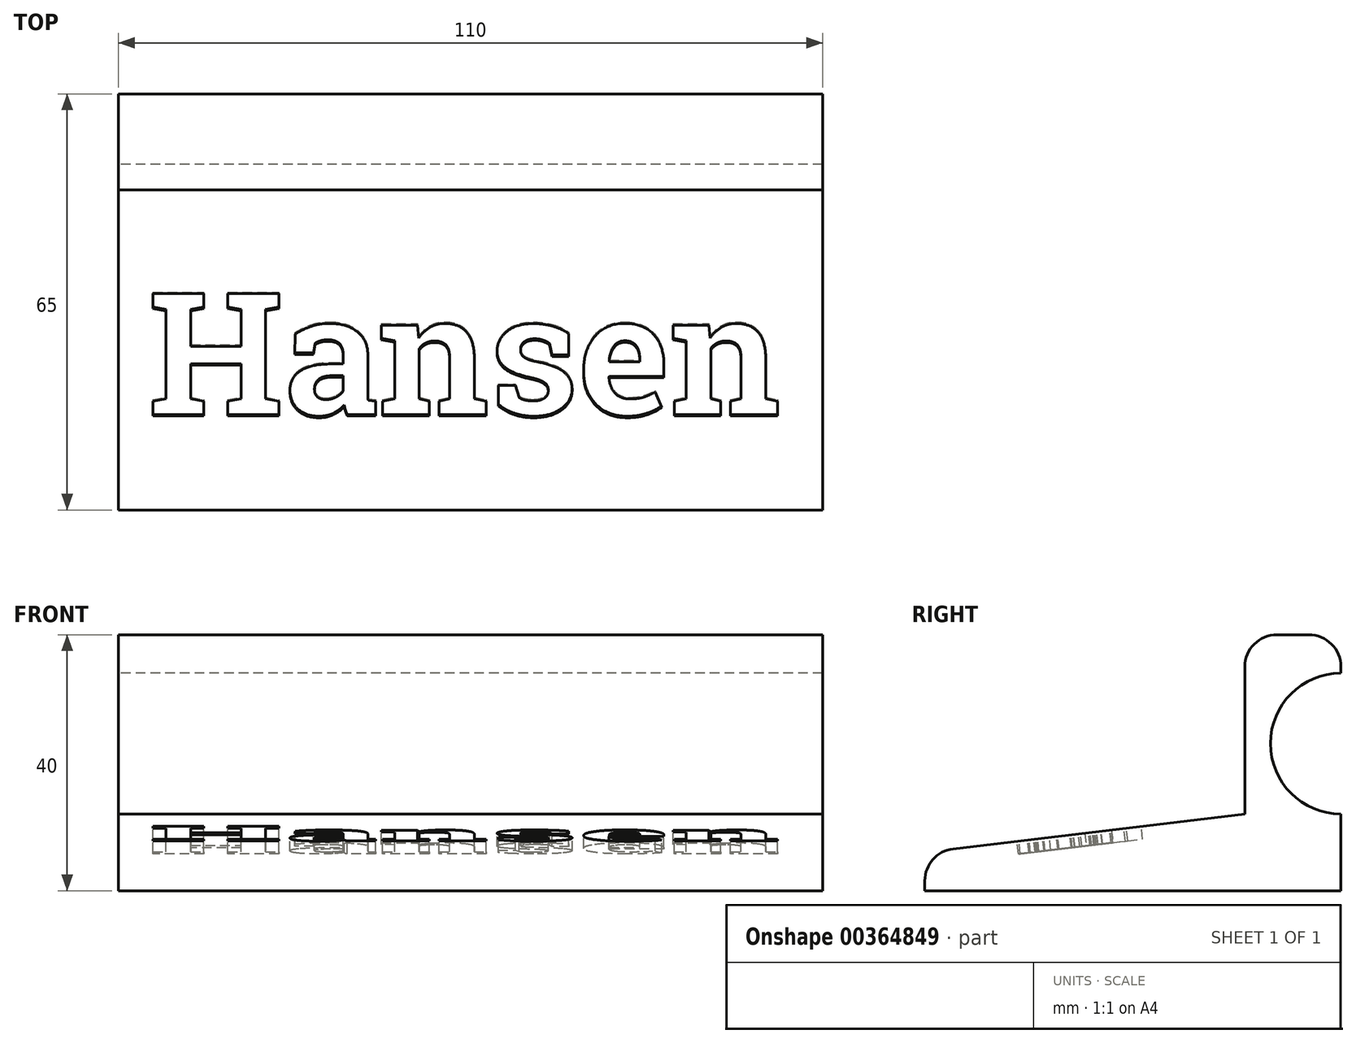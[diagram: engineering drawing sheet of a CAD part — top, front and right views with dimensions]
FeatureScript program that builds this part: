
annotation { "Feature Type Name" : "Feature", "Feature Type Description" : "" }
export const myFeature = defineFeature(function(context is Context, id is Id, definition is map)
    precondition{}
    {
        {
            var Q0;
            Q0=qCreatedBy(makeId("Front.planeOp"),FACE);
            var sketch = newSketch(context, id + "F0", { "sketchPlane" : qUnion([Q0])});
            skLineSegment(sketch, "E0.bottom", {"start": v(0, 0) * mm, "end": v(110, 0) * mm});
            skLineSegment(sketch, "E0.top", {"start": v(0, 40) * mm, "end": v(110, 40) * mm});
            skLineSegment(sketch, "E0.left", {"start": v(0, 0) * mm, "end": v(0, 40) * mm});
            skLineSegment(sketch, "E0.right", {"start": v(110, 0) * mm, "end": v(110, 40) * mm});
            skSolve(sketch);
        }
        {
            var Q0;
            Q0=makeQuery(id+"F0.imprint","IMPRINT",FACE,{"disambiguationData":[TD([[makeQuery(id+"F0.imprint","IMPRINT",EDGE,{"derivedFrom":sQuery(id+"F0.wireOp",EDGE,"E0.bottom")}),1.0]])]});
            extrude(context, id + "F1", {"entities" : qUnion([Q0]), "depth" : 15 * mm});
        }
        {
            var Q0;
            Q0=makeQuery(id+"F1.opExtrude","SWEPT_FACE",FACE,{"disambiguationData":[OSD([sQuery(id+"F0.wireOp",EDGE,"E0.left")])]});
            var sketch = newSketch(context, id + "F2", { "sketchPlane" : qUnion([Q0])});
            skCircle(sketch, "E1", {"center": v(0, 23) * mm, "radius": 11 * mm});
            skLineSegment(sketch, "E2", {"start": v(0, 23) * mm, "end": v(0, 40) * mm});
            skSolve(sketch);
        }
        {
            var Q0;
            {var subQ0=sQuery(id+"F2.wireOp",EDGE,"E1");var subQ1=makeQuery(id+"F1.opExtrude","CAP_EDGE",EDGE,{"disambiguationData":[OSD([sQuery(id+"F0.wireOp",EDGE,"E0.left")])],"isStart":true});var subQ2=makeQuery(id+"F2.imprint","INTERSECT",VERTEX,{"disambiguationData":[OD(0.0)],"derivedFrom":[subQ1,subQ0]});Q0=makeQuery(id+"F2.imprint","IMPRINT",FACE,{"disambiguationData":[TD([[makeQuery(id+"F2.imprint","IMPRINT",EDGE,{"disambiguationData":[TD([[subQ2,-1.0]])],"derivedFrom":subQ0}),1.0]])]});}
            extrude(context, id + "F3", {"entities" : qUnion([Q0]), "operationType" : NewBodyOperationType.REMOVE, "oppositeDirection" : true, "depth" : 112 * mm});
        }
        {
            var Q0;
            Q0=makeQuery(id+"F1.opExtrude","SWEPT_FACE",FACE,{"disambiguationData":[OSD([sQuery(id+"F0.wireOp",EDGE,"E0.right")])]});
            var sketch = newSketch(context, id + "F4", { "sketchPlane" : qUnion([Q0])});
            skLineSegment(sketch, "E3.bottom", {"start": v(-15, 0) * mm, "end": v(-65, 0) * mm});
            skLineSegment(sketch, "E3.top", {"start": v(-15, 6) * mm, "end": v(-65, 6) * mm});
            skLineSegment(sketch, "E3.left", {"start": v(-15, 0) * mm, "end": v(-15, 6) * mm});
            skLineSegment(sketch, "E3.right", {"start": v(-65, 0) * mm, "end": v(-65, 6) * mm});
            skLineSegment(sketch, "E4", {"start": v(-15, 6) * mm, "end": v(-15, 12) * mm});
            skLineSegment(sketch, "E5", {"start": v(-65, 6) * mm, "end": v(-15, 12) * mm});
            skSolve(sketch);
        }
        {
            var Q0;
            Q0=makeQuery(id+"F4.imprint","IMPRINT",FACE,{"disambiguationData":[TD([[makeQuery(id+"F4.imprint","IMPRINT",EDGE,{"derivedFrom":sQuery(id+"F4.wireOp",EDGE,"E3.bottom")}),-1.0]])]});
            var Q1;
            Q1=makeQuery(id+"F4.imprint","IMPRINT",FACE,{"disambiguationData":[TD([[makeQuery(id+"F4.imprint","IMPRINT",EDGE,{"derivedFrom":sQuery(id+"F4.wireOp",EDGE,"E3.top")}),-1.0]])]});
            extrude(context, id + "F5", {"entities" : qUnion([Q0, Q1]), "operationType" : NewBodyOperationType.ADD, "oppositeDirection" : true, "depth" : 110 * mm});
        }
        {
            var Q0;
            Q0=makeQuery(id+"F1.opExtrude","CAP_EDGE",EDGE,{"disambiguationData":[OSD([sQuery(id+"F0.wireOp",EDGE,"E0.top")])],"isStart":true});
            var Q1;
            Q1=makeQuery(id+"F1.opExtrude","CAP_EDGE",EDGE,{"disambiguationData":[OSD([sQuery(id+"F0.wireOp",EDGE,"E0.top")])],"isStart":false});
            var Q2;
            Q2=makeQuery(id+"F5.opExtrude","SWEPT_EDGE",EDGE,{"disambiguationData":[OSD([sQuery(id+"F4.wireOp",EDGE,"E3.top"),sQuery(id+"F4.wireOp",EDGE,"E3.right"),sQuery(id+"F4.wireOp",EDGE,"5C3QBkcI-RSvx-xwPt-XsPC-Cf5iGYV6OtuQ")])]});
            var Q3;
            Q3=makeQuery(id+"F5.opExtrude","SWEPT_EDGE",EDGE,{"disambiguationData":[OSD([sQuery(id+"F0.wireOp",EDGE,"E0.right"),sQuery(id+"F4.wireOp",EDGE,"E4"),sQuery(id+"F4.wireOp",EDGE,"5C3QBkcI-RSvx-xwPt-XsPC-Cf5iGYV6OtuQ")])]});
            fillet(context, id + "F6", {"entities" : qUnion([Q0, Q1, Q2, Q3]), "radius" : 5 * mm, "tangentPropagation" : true, "allowEdgeOverflow" : false});
        }
        {
            var Q0;
            Q0=makeQuery(id+"F5.opExtrude","SWEPT_FACE",FACE,{"disambiguationData":[OSD([sQuery(id+"F4.wireOp",EDGE,"E5")])]});
            var sketch = newSketch(context, id + "F7", { "sketchPlane" : qUnion([Q0])});
            skText(sketch, "E6", { "text": "Hansen", "fontName": "RobotoSlab-Bold.ttf"});
            const initialGuessF7  = {"E6": [0.00464, -0.04903, 1, 0, 0.01949]};
            skSetInitialGuess(sketch, initialGuessF7);
            skSolve(sketch);
        }
        {
            var Q0;
            Q0=makeQuery(id+"F7.imprint","IMPRINT",FACE,{"disambiguationData":[TD([[makeQuery(id+"F7.imprint","IMPRINT",EDGE,{"derivedFrom":sQuery(id+"F7.wireOp",EDGE,"E6.sketch_text.stroke-0")}),-1.0]])]});
            var Q1;
            Q1=makeQuery(id+"F7.imprint","IMPRINT",FACE,{"disambiguationData":[TD([[makeQuery(id+"F7.imprint","IMPRINT",EDGE,{"derivedFrom":sQuery(id+"F7.wireOp",EDGE,"E6.sketch_text.stroke-65")}),-1.0]])]});
            var Q2;
            Q2=makeQuery(id+"F7.imprint","IMPRINT",FACE,{"disambiguationData":[TD([[makeQuery(id+"F7.imprint","IMPRINT",EDGE,{"derivedFrom":sQuery(id+"F7.wireOp",EDGE,"E6.sketch_text.stroke-30")}),-1.0]])]});
            var Q3;
            Q3=makeQuery(id+"F7.imprint","IMPRINT",FACE,{"disambiguationData":[TD([[makeQuery(id+"F7.imprint","IMPRINT",EDGE,{"derivedFrom":sQuery(id+"F7.wireOp",EDGE,"E6.sketch_text.stroke-91")}),-1.0]])]});
            var Q4;
            Q4=makeQuery(id+"F7.imprint","IMPRINT",FACE,{"disambiguationData":[TD([[makeQuery(id+"F7.imprint","IMPRINT",EDGE,{"derivedFrom":sQuery(id+"F7.wireOp",EDGE,"E6.sketch_text.stroke-121")}),-1.0]])]});
            var Q5;
            Q5=makeQuery(id+"F7.imprint","IMPRINT",FACE,{"disambiguationData":[TD([[makeQuery(id+"F7.imprint","IMPRINT",EDGE,{"derivedFrom":sQuery(id+"F7.wireOp",EDGE,"E6.sketch_text.stroke-145")}),-1.0]])]});
            extrude(context, id + "F8", {"entities" : qUnion([Q0, Q1, Q2, Q3, Q4, Q5]), "operationType" : NewBodyOperationType.REMOVE, "oppositeDirection" : true, "depth" : 2 * mm});
        }
    });
